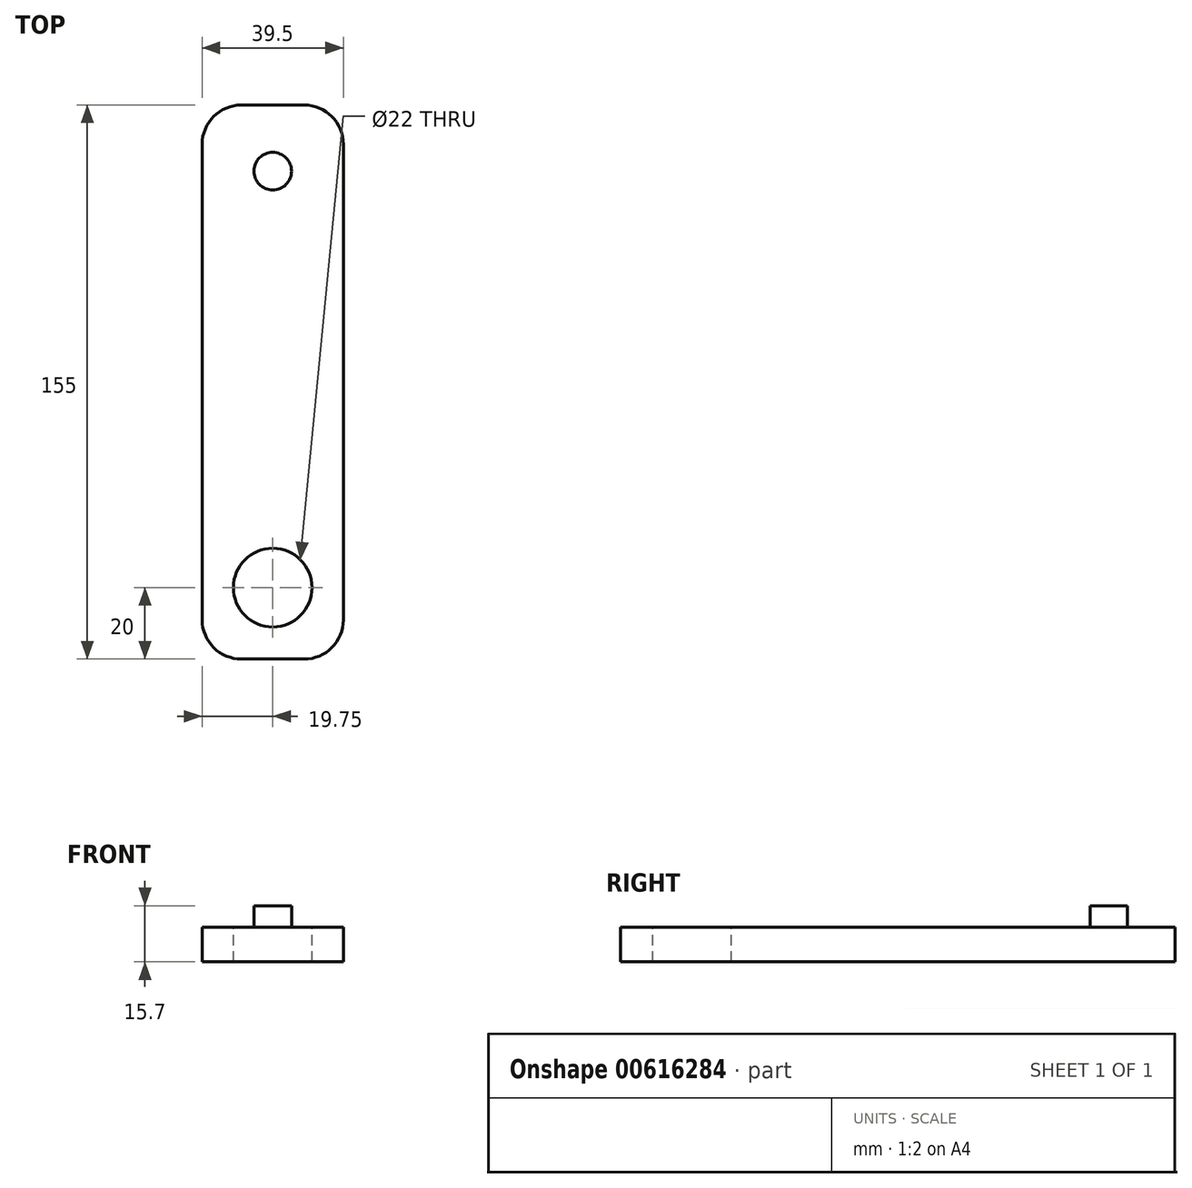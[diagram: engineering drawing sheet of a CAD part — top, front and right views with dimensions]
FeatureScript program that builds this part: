
annotation { "Feature Type Name" : "Feature", "Feature Type Description" : "" }
export const myFeature = defineFeature(function(context is Context, id is Id, definition is map)
    precondition{}
    {
        {
            var Q0;
            Q0=qCreatedBy(makeId("Top.planeOp"),FACE);
            var sketch = newSketch(context, id + "F0", { "sketchPlane" : qUnion([Q0])});
            skLineSegment(sketch, "E0.bottom", {"start": v(19.75, -77.5) * mm, "end": v(-19.75, -77.5) * mm});
            skLineSegment(sketch, "E0.top", {"start": v(19.75, 77.5) * mm, "end": v(-19.75, 77.5) * mm});
            skLineSegment(sketch, "E0.left", {"start": v(19.75, -77.5) * mm, "end": v(19.75, 77.5) * mm});
            skLineSegment(sketch, "E0.right", {"start": v(-19.75, -77.5) * mm, "end": v(-19.75, 77.5) * mm});
            skPoint(sketch, "E0.middle", {"position": v(0, 0) * mm});
            skSolve(sketch);
        }
        {
            var Q0;
            Q0=makeQuery(id+"F0.imprint","IMPRINT",FACE,{"disambiguationData":[TD([[makeQuery(id+"F0.imprint","IMPRINT",EDGE,{"derivedFrom":sQuery(id+"F0.wireOp",EDGE,"E0.bottom")}),-1.0]])]});
            extrude(context, id + "F1", {"entities" : qUnion([Q0]), "depth" : 9.7 * mm, "offsetDistance" : 25 * mm});
        }
        {
            var Q0;
            Q0=makeQuery(id+"F1.opExtrude","SWEPT_EDGE",EDGE,{"disambiguationData":[OSD([sQuery(id+"F0.wireOp",EDGE,"E0.top"),sQuery(id+"F0.wireOp",EDGE,"E0.right")])]});
            var Q1;
            Q1=makeQuery(id+"F1.opExtrude","SWEPT_EDGE",EDGE,{"disambiguationData":[OSD([sQuery(id+"F0.wireOp",EDGE,"E0.top"),sQuery(id+"F0.wireOp",EDGE,"E0.left")])]});
            var Q2;
            Q2=makeQuery(id+"F1.opExtrude","SWEPT_EDGE",EDGE,{"disambiguationData":[OSD([sQuery(id+"F0.wireOp",EDGE,"E0.bottom"),sQuery(id+"F0.wireOp",EDGE,"E0.left")])]});
            var Q3;
            Q3=makeQuery(id+"F1.opExtrude","SWEPT_EDGE",EDGE,{"disambiguationData":[OSD([sQuery(id+"F0.wireOp",EDGE,"E0.bottom"),sQuery(id+"F0.wireOp",EDGE,"E0.right")])]});
            fillet(context, id + "F2", {"entities" : qUnion([Q0, Q1, Q2, Q3]), "radius" : 11 * mm, "tangentPropagation" : true, "allowEdgeOverflow" : false});
        }
        {
            var Q0;
            Q0=makeQuery(id+"F1.opExtrude","CAP_FACE",FACE,{"disambiguationData":[OSD([sQuery(id+"F0.wireOp",EDGE,"E0.bottom"),sQuery(id+"F0.wireOp",EDGE,"E0.top"),sQuery(id+"F0.wireOp",EDGE,"E0.left"),sQuery(id+"F0.wireOp",EDGE,"E0.right")])],"isStart":false});
            var sketch = newSketch(context, id + "F3", { "sketchPlane" : qUnion([Q0])});
            skCircle(sketch, "E1", {"center": v(0, -57.5) * mm, "radius": 11 * mm});
            skSolve(sketch);
        }
        {
            var Q0;
            Q0=makeQuery(id+"F3.imprint","IMPRINT",FACE,{"disambiguationData":[TD([[makeQuery(id+"F3.imprint","IMPRINT",EDGE,{"derivedFrom":sQuery(id+"F3.wireOp",EDGE,"E1")}),1.0]])]});
            extrude(context, id + "F4", {"entities" : qUnion([Q0]), "operationType" : NewBodyOperationType.REMOVE, "endBound" : BoundingType.THROUGH_ALL, "oppositeDirection" : true, "depth" : 25 * mm, "offsetDistance" : 25 * mm});
        }
        {
            var Q0;
            Q0=makeQuery(id+"F1.opExtrude","CAP_FACE",FACE,{"disambiguationData":[OSD([sQuery(id+"F0.wireOp",EDGE,"E0.bottom"),sQuery(id+"F0.wireOp",EDGE,"E0.top"),sQuery(id+"F0.wireOp",EDGE,"E0.left"),sQuery(id+"F0.wireOp",EDGE,"E0.right")])],"isStart":false});
            var sketch = newSketch(context, id + "F5", { "sketchPlane" : qUnion([Q0])});
            skCircle(sketch, "E2", {"center": v(0, 59) * mm, "radius": 5.25 * mm});
            skSolve(sketch);
        }
        {
            var Q0;
            Q0=makeQuery(id+"F5.imprint","IMPRINT",FACE,{"disambiguationData":[TD([[makeQuery(id+"F5.imprint","IMPRINT",EDGE,{"derivedFrom":sQuery(id+"F5.wireOp",EDGE,"E2")}),1.0]])]});
            extrude(context, id + "F6", {"entities" : qUnion([Q0]), "operationType" : NewBodyOperationType.ADD, "depth" : 6 * mm, "offsetDistance" : 25 * mm});
        }
    });
